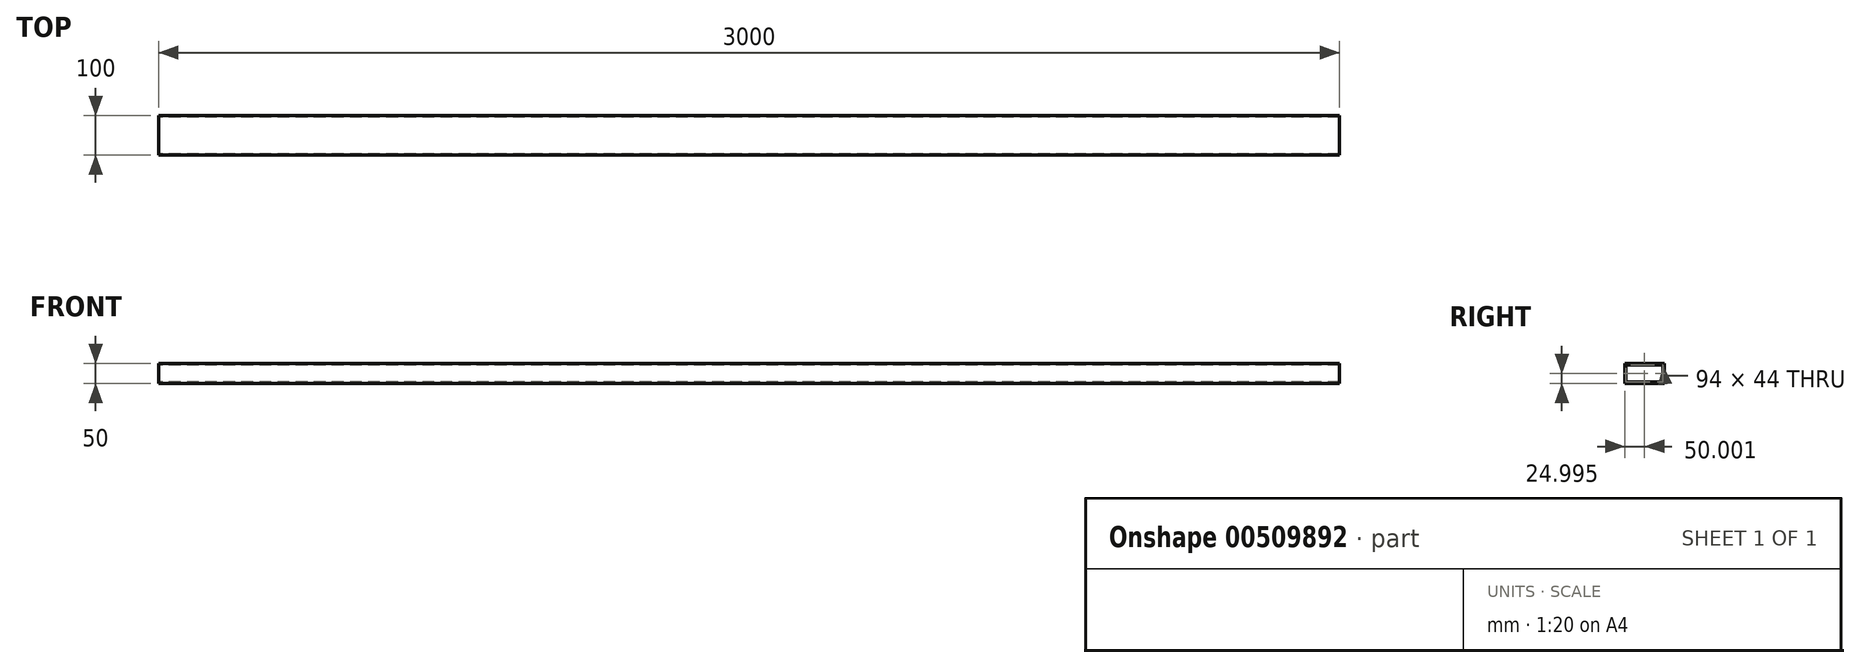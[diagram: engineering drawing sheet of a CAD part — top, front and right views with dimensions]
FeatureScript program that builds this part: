
annotation { "Feature Type Name" : "Feature", "Feature Type Description" : "" }
export const myFeature = defineFeature(function(context is Context, id is Id, definition is map)
    precondition{}
    {
        {
            var Q0;
            Q0=qCreatedBy(makeId("Right.planeOp"),FACE);
            var sketch = newSketch(context, id + "F0", { "sketchPlane" : qUnion([Q0])});
            skLineSegment(sketch, "E0.bottom", {"start": v(55.08, -16.73) * mm, "end": v(-44.92, -16.73) * mm});
            skLineSegment(sketch, "E0.top", {"start": v(55.08, 33.27) * mm, "end": v(-44.92, 33.27) * mm});
            skLineSegment(sketch, "E0.left", {"start": v(55.08, -16.73) * mm, "end": v(55.08, 33.27) * mm});
            skLineSegment(sketch, "E0.right", {"start": v(-44.92, -16.73) * mm, "end": v(-44.92, 33.27) * mm});
            skPoint(sketch, "E0.middle", {"position": v(5.08, 8.27) * mm});
            skLineSegment(sketch, "E1.bottom", {"start": v(52.08, -13.73) * mm, "end": v(-41.92, -13.73) * mm});
            skLineSegment(sketch, "E1.top", {"start": v(52.08, 30.27) * mm, "end": v(-41.92, 30.27) * mm});
            skLineSegment(sketch, "E1.left", {"start": v(52.08, -13.73) * mm, "end": v(52.08, 30.27) * mm});
            skLineSegment(sketch, "E1.right", {"start": v(-41.92, -13.73) * mm, "end": v(-41.92, 30.27) * mm});
            skSolve(sketch);
        }
        {
            var Q0;
            Q0=makeQuery(id+"F0.imprint","IMPRINT",FACE,{"disambiguationData":[TD([[makeQuery(id+"F0.imprint","IMPRINT",EDGE,{"derivedFrom":sQuery(id+"F0.wireOp",EDGE,"E0.bottom")}),-1.0]])]});
            extrude(context, id + "F1", {"entities" : qUnion([Q0]), "depth" : 3000 * mm});
        }
    });
